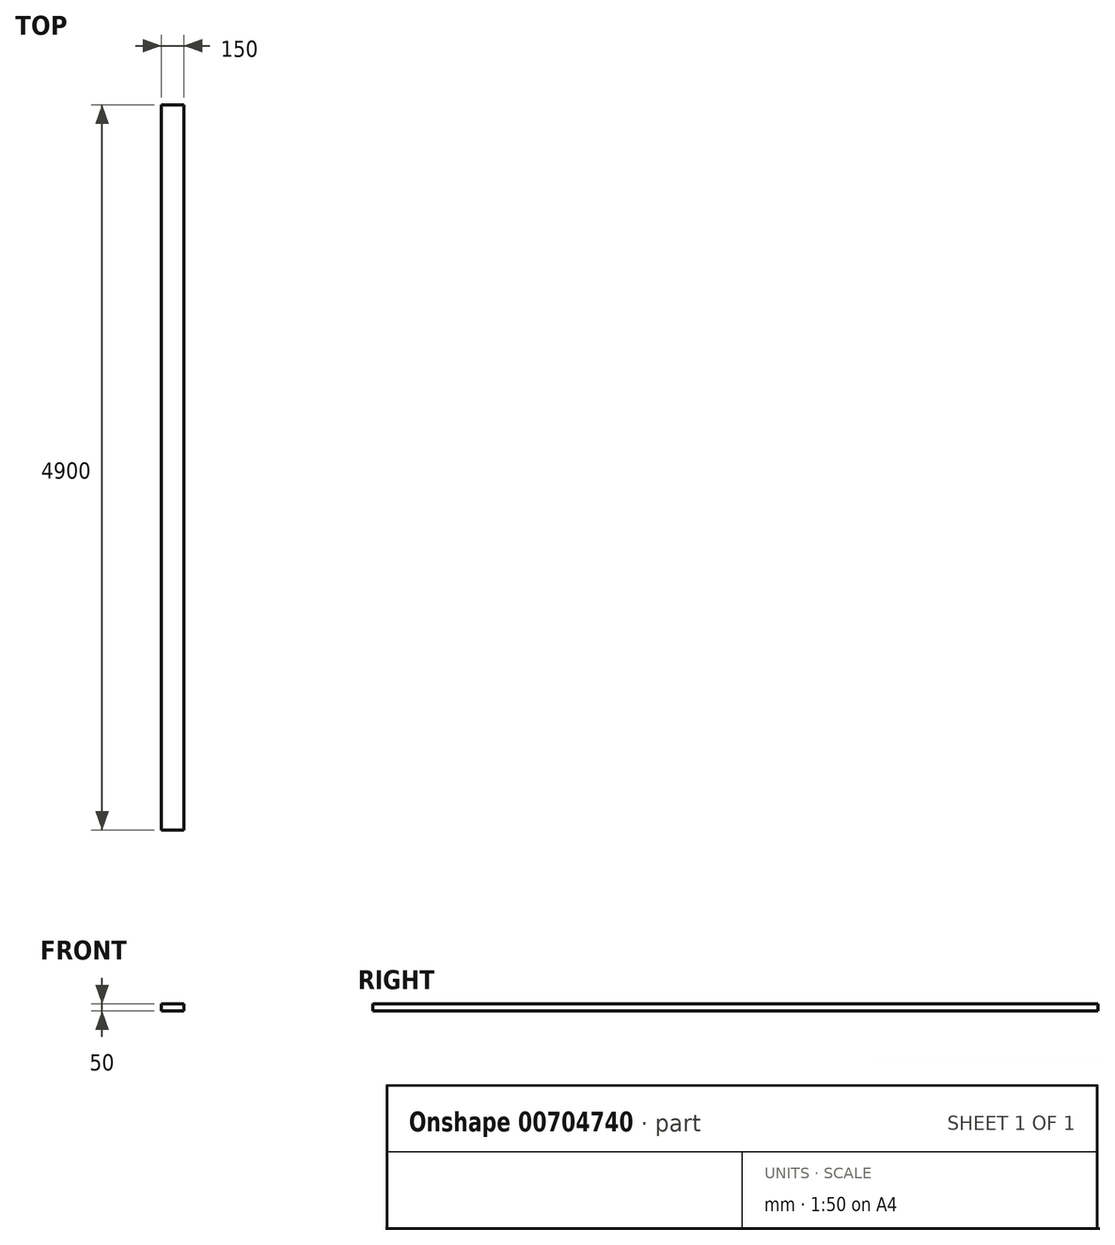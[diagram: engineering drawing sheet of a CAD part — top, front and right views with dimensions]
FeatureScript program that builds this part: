
annotation { "Feature Type Name" : "Feature", "Feature Type Description" : "" }
export const myFeature = defineFeature(function(context is Context, id is Id, definition is map)
    precondition{}
    {
        {
            var Q0;
            Q0=qCreatedBy(makeId("Front.planeOp"),FACE);
            var sketch = newSketch(context, id + "F0", { "sketchPlane" : qUnion([Q0])});
            skLineSegment(sketch, "E0.bottom", {"start": v(0, 0) * mm, "end": v(150, 0) * mm});
            skLineSegment(sketch, "E0.top", {"start": v(0, 50) * mm, "end": v(150, 50) * mm});
            skLineSegment(sketch, "E0.left", {"start": v(0, 0) * mm, "end": v(0, 50) * mm});
            skLineSegment(sketch, "E0.right", {"start": v(150, 0) * mm, "end": v(150, 50) * mm});
            skSolve(sketch);
        }
        {
            var Q0;
            Q0 = qSketchRegion(id + "F0", true);
            extrude(context, id + "F1", {"entities" : qUnion([Q0]), "depth" : 4900 * mm, "offsetDistance" : 25 * mm});
        }
    });
